# Revit family: Faucet_Touchless-Lavatory-KOHLER-Oblo-K-24270T_1
name_source: partatom
category: Plumbing Fixtures
units: mm (PartAtom-declared; Revit-internal decimal feet)

## family parameters
Cut with Voids When Loaded = No
Host = Face
OmniClass Number = 23.31.11.00
OmniClass Title = Faucets
Part Type = Normal
Room Calculation Point = No
Round Connector Dimension = Use Diameter
Shared = No

## types (3) — shared parameters
ADA Compliant = No
Apparent Load = 0 VA
Assembly Code = D2010
CW Connection = Yes
Cold Water Inlet = Cold Water Inlet
Date Modified = 12/08/2022
Default Elevation = 36"
Drain Included = Yes
Electrical Connector = Yes
Electrical Note = One Dedicated Circuit Required
Finish = Kohler-Metal-CP-Polished_Chrome
HW Connection = No
Height = 8 1/16"
Hot Water Inlet = Hot Water Inlet
Length = 5 9/16"
Manufacturer = Kohler Co.
Master Format 2014 = 22 41 39
Master Format 2014 Name = Residential Faucets, Supplies, and Trim
Material = Premium Metal Construction
Pressure = 0.00 psi
Product Name = Oblo
Spout Reach = 5 9/16"
URL = http://www.kohler.com.cn
Vent Connection = No
Voltage = 220 V
Waste Connection = No
Waste Water Outlet = Waste Water Outlet
WaterSense Certified = No
Width = 2 5/16"

## per-type parameters (varying)
| type | Description | Flow Rate | Model | Type |
| 0.5 GPM, CP-Polished Chrome | Deck Mount Sensor Faucet Cold 0.5 GPM SP | 1 GPM | K-24270T-NW-CP | 1 |
| 0.35 GPM, CP-Polished Chrome | Deck Mount Sensor Faucet Cold 0.35 GPM SP | 0 GPM | K-24270T-NWS3-CP | 2 |
| 0.26 GPM, CP-Polished Chrome | Deck Mount Sensor Faucet Cold 0.26 GPM SP | 0 GPM | K-24270T-NWS5-CP | 3 |

## geometry (parser evidence)
native form markers: Sweep x4
no freeform markers — native parametric forms only
